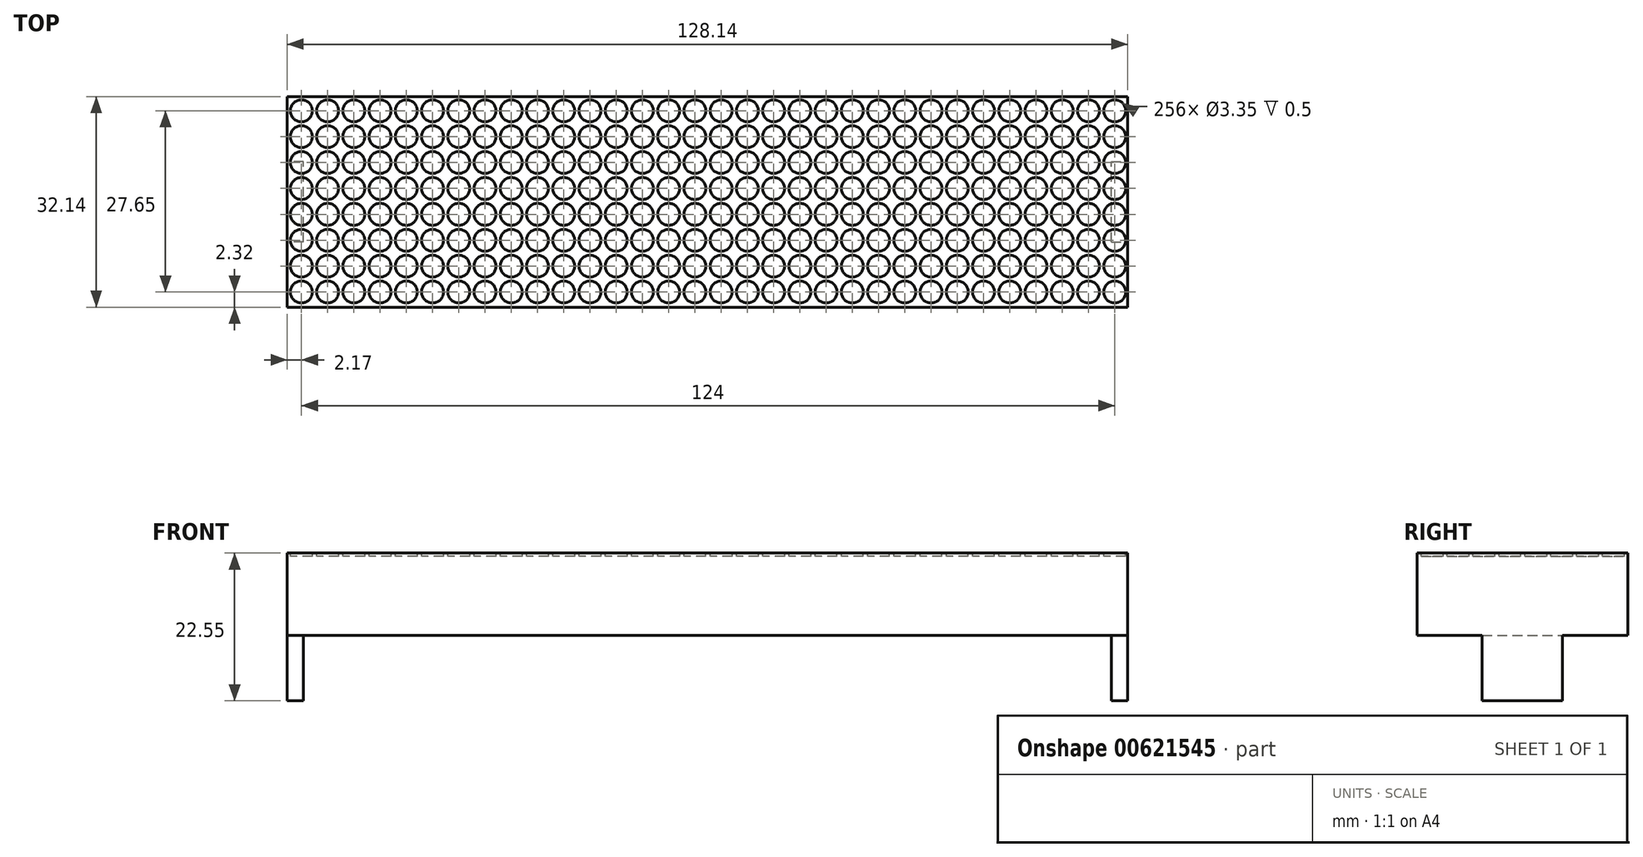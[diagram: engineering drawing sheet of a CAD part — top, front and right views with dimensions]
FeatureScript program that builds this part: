
annotation { "Feature Type Name" : "Feature", "Feature Type Description" : "" }
export const myFeature = defineFeature(function(context is Context, id is Id, definition is map)
    precondition{}
    {
        {
            var Q0;
            Q0=qCreatedBy(makeId("Top.planeOp"),FACE);
            var sketch = newSketch(context, id + "F0", { "sketchPlane" : qUnion([Q0])});
            skLineSegment(sketch, "E0.bottom", {"start": v(64.08, -16.07) * mm, "end": v(-64.08, -16.08) * mm});
            skLineSegment(sketch, "E0.top", {"start": v(64.08, 16.08) * mm, "end": v(-64.08, 16.07) * mm});
            skLineSegment(sketch, "E0.left", {"start": v(64.08, -16.07) * mm, "end": v(64.08, 16.08) * mm});
            skLineSegment(sketch, "E0.right", {"start": v(-64.08, -16.08) * mm, "end": v(-64.08, 16.07) * mm});
            skPoint(sketch, "E0.middle", {"position": v(0, 0) * mm});
            skSolve(sketch);
        }
        {
            var Q0;
            Q0=makeQuery(id+"F0.imprint","IMPRINT",FACE,{"disambiguationData":[TD([[makeQuery(id+"F0.imprint","IMPRINT",EDGE,{"derivedFrom":sQuery(id+"F0.wireOp",EDGE,"E0.bottom")}),-1.0]])]});
            extrude(context, id + "F1", {"entities" : qUnion([Q0]), "depth" : 12.55 * mm, "offsetDistance" : 25 * mm});
        }
        {
            var Q0;
            Q0=makeQuery(id+"F1.opExtrude","CAP_FACE",FACE,{"disambiguationData":[OSD([sQuery(id+"F0.wireOp",EDGE,"E0.bottom"),sQuery(id+"F0.wireOp",EDGE,"E0.top"),sQuery(id+"F0.wireOp",EDGE,"E0.left"),sQuery(id+"F0.wireOp",EDGE,"E0.right")])],"isStart":true});
            var sketch = newSketch(context, id + "F2", { "sketchPlane" : qUnion([Q0])});
            skLineSegment(sketch, "E1.bottom", {"start": v(-61.58, 6.12) * mm, "end": v(-64.08, 6.12) * mm});
            skLineSegment(sketch, "E1.top", {"start": v(-61.58, -6.13) * mm, "end": v(-64.08, -6.13) * mm});
            skLineSegment(sketch, "E1.left", {"start": v(-61.58, 6.12) * mm, "end": v(-61.58, -6.13) * mm});
            skLineSegment(sketch, "E1.right", {"start": v(-64.08, 6.12) * mm, "end": v(-64.08, -6.13) * mm});
            skPoint(sketch, "E1.middle", {"position": v(-62.83, 0) * mm});
            skPoint(sketch, "E2.MirrorP", {"position": v(62.83, 0) * mm});
            skLineSegment(sketch, "E3.MirrorCS", {"start": v(61.58, 6.12) * mm, "end": v(64.08, 6.12) * mm});
            skLineSegment(sketch, "E4.MirrorCS", {"start": v(61.58, -6.13) * mm, "end": v(64.08, -6.13) * mm});
            skLineSegment(sketch, "E5.MirrorCS", {"start": v(61.58, 6.12) * mm, "end": v(61.58, -6.13) * mm});
            skLineSegment(sketch, "E6.MirrorCS", {"start": v(64.08, 6.12) * mm, "end": v(64.08, -6.13) * mm});
            skSolve(sketch);
        }
        {
            var Q0;
            Q0 = qSketchRegion(id + "F2", true);
            extrude(context, id + "F3", {"entities" : qUnion([Q0]), "operationType" : NewBodyOperationType.ADD, "depth" : 10 * mm, "offsetDistance" : 25 * mm});
        }
        {
            var Q0;
            Q0=makeQuery(id+"F1.opExtrude","CAP_FACE",FACE,{"disambiguationData":[OSD([sQuery(id+"F0.wireOp",EDGE,"E0.bottom"),sQuery(id+"F0.wireOp",EDGE,"E0.top"),sQuery(id+"F0.wireOp",EDGE,"E0.left"),sQuery(id+"F0.wireOp",EDGE,"E0.right")])],"isStart":false});
            var sketch = newSketch(context, id + "F4", { "sketchPlane" : qUnion([Q0])});
            skCircle(sketch, "E7", {"center": v(-61.9, 13.9) * mm, "radius": 1.68 * mm});
            skCircle(sketch, "E8.0.1.0", {"center": v(-61.9, 9.95) * mm, "radius": 1.68 * mm});
            skCircle(sketch, "E8.0.2.0", {"center": v(-61.9, 6) * mm, "radius": 1.68 * mm});
            skCircle(sketch, "E8.0.3.0", {"center": v(-61.9, 2.05) * mm, "radius": 1.68 * mm});
            skCircle(sketch, "E8.0.4.0", {"center": v(-61.9, -1.9) * mm, "radius": 1.68 * mm});
            skCircle(sketch, "E8.0.5.0", {"center": v(-61.9, -5.85) * mm, "radius": 1.68 * mm});
            skCircle(sketch, "E8.0.6.0", {"center": v(-61.9, -9.8) * mm, "radius": 1.68 * mm});
            skCircle(sketch, "E8.0.7.0", {"center": v(-61.9, -13.75) * mm, "radius": 1.68 * mm});
            skCircle(sketch, "E8.1.0.0", {"center": v(-57.9, 13.9) * mm, "radius": 1.68 * mm});
            skCircle(sketch, "E8.1.1.0", {"center": v(-57.9, 9.95) * mm, "radius": 1.68 * mm});
            skCircle(sketch, "E8.1.2.0", {"center": v(-57.9, 6) * mm, "radius": 1.68 * mm});
            skCircle(sketch, "E8.1.3.0", {"center": v(-57.9, 2.05) * mm, "radius": 1.68 * mm});
            skCircle(sketch, "E8.1.4.0", {"center": v(-57.9, -1.9) * mm, "radius": 1.68 * mm});
            skCircle(sketch, "E8.1.5.0", {"center": v(-57.9, -5.85) * mm, "radius": 1.68 * mm});
            skCircle(sketch, "E8.1.6.0", {"center": v(-57.9, -9.8) * mm, "radius": 1.68 * mm});
            skCircle(sketch, "E8.1.7.0", {"center": v(-57.9, -13.75) * mm, "radius": 1.68 * mm});
            skCircle(sketch, "E8.2.0.0", {"center": v(-53.9, 13.9) * mm, "radius": 1.68 * mm});
            skCircle(sketch, "E8.2.1.0", {"center": v(-53.9, 9.95) * mm, "radius": 1.68 * mm});
            skCircle(sketch, "E8.2.2.0", {"center": v(-53.9, 6) * mm, "radius": 1.68 * mm});
            skCircle(sketch, "E8.2.3.0", {"center": v(-53.9, 2.05) * mm, "radius": 1.68 * mm});
            skCircle(sketch, "E8.2.4.0", {"center": v(-53.9, -1.9) * mm, "radius": 1.68 * mm});
            skCircle(sketch, "E8.2.5.0", {"center": v(-53.9, -5.85) * mm, "radius": 1.68 * mm});
            skCircle(sketch, "E8.2.6.0", {"center": v(-53.9, -9.8) * mm, "radius": 1.68 * mm});
            skCircle(sketch, "E8.2.7.0", {"center": v(-53.9, -13.75) * mm, "radius": 1.68 * mm});
            skLineSegment(sketch, "E8.direction1", {"start": v(-61.9, 13.9) * mm, "end": v(-57.9, 13.9) * mm, "construction": true});
            skLineSegment(sketch, "E8.direction2", {"start": v(-61.9, 13.9) * mm, "end": v(-61.9, 9.95) * mm, "construction": true});
            skCircle(sketch, "E9.0.3.0", {"center": v(-49.9, 13.9) * mm, "radius": 1.68 * mm});
            skCircle(sketch, "E9.0.3.1", {"center": v(-49.9, 9.95) * mm, "radius": 1.68 * mm});
            skCircle(sketch, "E9.0.3.2", {"center": v(-49.9, 6) * mm, "radius": 1.68 * mm});
            skCircle(sketch, "E9.0.3.3", {"center": v(-49.9, 2.05) * mm, "radius": 1.68 * mm});
            skCircle(sketch, "E9.0.3.4", {"center": v(-49.9, -1.9) * mm, "radius": 1.68 * mm});
            skCircle(sketch, "E9.0.3.5", {"center": v(-49.9, -5.85) * mm, "radius": 1.68 * mm});
            skCircle(sketch, "E9.0.3.6", {"center": v(-49.9, -9.8) * mm, "radius": 1.68 * mm});
            skCircle(sketch, "E9.0.3.7", {"center": v(-49.9, -13.75) * mm, "radius": 1.68 * mm});
            skCircle(sketch, "E9.0.4.0", {"center": v(-45.9, 13.9) * mm, "radius": 1.68 * mm});
            skCircle(sketch, "E9.0.4.1", {"center": v(-45.9, 9.95) * mm, "radius": 1.68 * mm});
            skCircle(sketch, "E9.0.4.2", {"center": v(-45.9, 6) * mm, "radius": 1.68 * mm});
            skCircle(sketch, "E9.0.4.3", {"center": v(-45.9, 2.05) * mm, "radius": 1.68 * mm});
            skCircle(sketch, "E9.0.4.4", {"center": v(-45.9, -1.9) * mm, "radius": 1.68 * mm});
            skCircle(sketch, "E9.0.4.5", {"center": v(-45.9, -5.85) * mm, "radius": 1.68 * mm});
            skCircle(sketch, "E9.0.4.6", {"center": v(-45.9, -9.8) * mm, "radius": 1.68 * mm});
            skCircle(sketch, "E9.0.4.7", {"center": v(-45.9, -13.75) * mm, "radius": 1.68 * mm});
            skCircle(sketch, "E9.0.5.0", {"center": v(-41.9, 13.9) * mm, "radius": 1.68 * mm});
            skCircle(sketch, "E9.0.5.1", {"center": v(-41.9, 9.95) * mm, "radius": 1.68 * mm});
            skCircle(sketch, "E9.0.5.2", {"center": v(-41.9, 6) * mm, "radius": 1.68 * mm});
            skCircle(sketch, "E9.0.5.3", {"center": v(-41.9, 2.05) * mm, "radius": 1.68 * mm});
            skCircle(sketch, "E9.0.5.4", {"center": v(-41.9, -1.9) * mm, "radius": 1.68 * mm});
            skCircle(sketch, "E9.0.5.5", {"center": v(-41.9, -5.85) * mm, "radius": 1.68 * mm});
            skCircle(sketch, "E9.0.5.6", {"center": v(-41.9, -9.8) * mm, "radius": 1.68 * mm});
            skCircle(sketch, "E9.0.5.7", {"center": v(-41.9, -13.75) * mm, "radius": 1.68 * mm});
            skCircle(sketch, "E9.0.6.0", {"center": v(-37.9, 13.9) * mm, "radius": 1.68 * mm});
            skCircle(sketch, "E9.0.6.1", {"center": v(-37.9, 9.95) * mm, "radius": 1.68 * mm});
            skCircle(sketch, "E9.0.6.2", {"center": v(-37.9, 6) * mm, "radius": 1.68 * mm});
            skCircle(sketch, "E9.0.6.3", {"center": v(-37.9, 2.05) * mm, "radius": 1.68 * mm});
            skCircle(sketch, "E9.0.6.4", {"center": v(-37.9, -1.9) * mm, "radius": 1.68 * mm});
            skCircle(sketch, "E9.0.6.5", {"center": v(-37.9, -5.85) * mm, "radius": 1.68 * mm});
            skCircle(sketch, "E9.0.6.6", {"center": v(-37.9, -9.8) * mm, "radius": 1.68 * mm});
            skCircle(sketch, "E9.0.6.7", {"center": v(-37.9, -13.75) * mm, "radius": 1.68 * mm});
            skCircle(sketch, "E9.0.7.0", {"center": v(-33.9, 13.9) * mm, "radius": 1.68 * mm});
            skCircle(sketch, "E9.0.7.1", {"center": v(-33.9, 9.95) * mm, "radius": 1.68 * mm});
            skCircle(sketch, "E9.0.7.2", {"center": v(-33.9, 6) * mm, "radius": 1.68 * mm});
            skCircle(sketch, "E9.0.7.3", {"center": v(-33.9, 2.05) * mm, "radius": 1.68 * mm});
            skCircle(sketch, "E9.0.7.4", {"center": v(-33.9, -1.9) * mm, "radius": 1.68 * mm});
            skCircle(sketch, "E9.0.7.5", {"center": v(-33.9, -5.85) * mm, "radius": 1.68 * mm});
            skCircle(sketch, "E9.0.7.6", {"center": v(-33.9, -9.8) * mm, "radius": 1.68 * mm});
            skCircle(sketch, "E9.0.7.7", {"center": v(-33.9, -13.75) * mm, "radius": 1.68 * mm});
            skCircle(sketch, "E9.0.8.0", {"center": v(-29.9, 13.9) * mm, "radius": 1.68 * mm});
            skCircle(sketch, "E9.0.8.1", {"center": v(-29.9, 9.95) * mm, "radius": 1.68 * mm});
            skCircle(sketch, "E9.0.8.2", {"center": v(-29.9, 6) * mm, "radius": 1.68 * mm});
            skCircle(sketch, "E9.0.8.3", {"center": v(-29.9, 2.05) * mm, "radius": 1.68 * mm});
            skCircle(sketch, "E9.0.8.4", {"center": v(-29.9, -1.9) * mm, "radius": 1.68 * mm});
            skCircle(sketch, "E9.0.8.5", {"center": v(-29.9, -5.85) * mm, "radius": 1.68 * mm});
            skCircle(sketch, "E9.0.8.6", {"center": v(-29.9, -9.8) * mm, "radius": 1.68 * mm});
            skCircle(sketch, "E9.0.8.7", {"center": v(-29.9, -13.75) * mm, "radius": 1.68 * mm});
            skCircle(sketch, "E9.0.9.0", {"center": v(-25.9, 13.9) * mm, "radius": 1.68 * mm});
            skCircle(sketch, "E9.0.9.1", {"center": v(-25.9, 9.95) * mm, "radius": 1.68 * mm});
            skCircle(sketch, "E9.0.9.2", {"center": v(-25.9, 6) * mm, "radius": 1.68 * mm});
            skCircle(sketch, "E9.0.9.3", {"center": v(-25.9, 2.05) * mm, "radius": 1.68 * mm});
            skCircle(sketch, "E9.0.9.4", {"center": v(-25.9, -1.9) * mm, "radius": 1.68 * mm});
            skCircle(sketch, "E9.0.9.5", {"center": v(-25.9, -5.85) * mm, "radius": 1.68 * mm});
            skCircle(sketch, "E9.0.9.6", {"center": v(-25.9, -9.8) * mm, "radius": 1.68 * mm});
            skCircle(sketch, "E9.0.9.7", {"center": v(-25.9, -13.75) * mm, "radius": 1.68 * mm});
            skCircle(sketch, "E9.0.10.0", {"center": v(-21.9, 13.9) * mm, "radius": 1.68 * mm});
            skCircle(sketch, "E9.0.10.1", {"center": v(-21.9, 9.95) * mm, "radius": 1.68 * mm});
            skCircle(sketch, "E9.0.10.2", {"center": v(-21.9, 6) * mm, "radius": 1.68 * mm});
            skCircle(sketch, "E9.0.10.3", {"center": v(-21.9, 2.05) * mm, "radius": 1.68 * mm});
            skCircle(sketch, "E9.0.10.4", {"center": v(-21.9, -1.9) * mm, "radius": 1.68 * mm});
            skCircle(sketch, "E9.0.10.5", {"center": v(-21.9, -5.85) * mm, "radius": 1.68 * mm});
            skCircle(sketch, "E9.0.10.6", {"center": v(-21.9, -9.8) * mm, "radius": 1.68 * mm});
            skCircle(sketch, "E9.0.10.7", {"center": v(-21.9, -13.75) * mm, "radius": 1.68 * mm});
            skCircle(sketch, "E9.0.11.0", {"center": v(-17.9, 13.9) * mm, "radius": 1.68 * mm});
            skCircle(sketch, "E9.0.11.1", {"center": v(-17.9, 9.95) * mm, "radius": 1.68 * mm});
            skCircle(sketch, "E9.0.11.2", {"center": v(-17.9, 6) * mm, "radius": 1.68 * mm});
            skCircle(sketch, "E9.0.11.3", {"center": v(-17.9, 2.05) * mm, "radius": 1.68 * mm});
            skCircle(sketch, "E9.0.11.4", {"center": v(-17.9, -1.9) * mm, "radius": 1.68 * mm});
            skCircle(sketch, "E9.0.11.5", {"center": v(-17.9, -5.85) * mm, "radius": 1.68 * mm});
            skCircle(sketch, "E9.0.11.6", {"center": v(-17.9, -9.8) * mm, "radius": 1.68 * mm});
            skCircle(sketch, "E9.0.11.7", {"center": v(-17.9, -13.75) * mm, "radius": 1.68 * mm});
            skCircle(sketch, "E9.0.12.0", {"center": v(-13.9, 13.9) * mm, "radius": 1.68 * mm});
            skCircle(sketch, "E9.0.12.1", {"center": v(-13.9, 9.95) * mm, "radius": 1.68 * mm});
            skCircle(sketch, "E9.0.12.2", {"center": v(-13.9, 6) * mm, "radius": 1.68 * mm});
            skCircle(sketch, "E9.0.12.3", {"center": v(-13.9, 2.05) * mm, "radius": 1.68 * mm});
            skCircle(sketch, "E9.0.12.4", {"center": v(-13.9, -1.9) * mm, "radius": 1.68 * mm});
            skCircle(sketch, "E9.0.12.5", {"center": v(-13.9, -5.85) * mm, "radius": 1.68 * mm});
            skCircle(sketch, "E9.0.12.6", {"center": v(-13.9, -9.8) * mm, "radius": 1.68 * mm});
            skCircle(sketch, "E9.0.12.7", {"center": v(-13.9, -13.75) * mm, "radius": 1.68 * mm});
            skCircle(sketch, "E9.0.13.0", {"center": v(-9.9, 13.9) * mm, "radius": 1.68 * mm});
            skCircle(sketch, "E9.0.13.1", {"center": v(-9.9, 9.95) * mm, "radius": 1.68 * mm});
            skCircle(sketch, "E9.0.13.2", {"center": v(-9.9, 6) * mm, "radius": 1.68 * mm});
            skCircle(sketch, "E9.0.13.3", {"center": v(-9.9, 2.05) * mm, "radius": 1.68 * mm});
            skCircle(sketch, "E9.0.13.4", {"center": v(-9.9, -1.9) * mm, "radius": 1.68 * mm});
            skCircle(sketch, "E9.0.13.5", {"center": v(-9.9, -5.85) * mm, "radius": 1.68 * mm});
            skCircle(sketch, "E9.0.13.6", {"center": v(-9.9, -9.8) * mm, "radius": 1.68 * mm});
            skCircle(sketch, "E9.0.13.7", {"center": v(-9.9, -13.75) * mm, "radius": 1.68 * mm});
            skCircle(sketch, "E9.0.14.0", {"center": v(-5.9, 13.9) * mm, "radius": 1.68 * mm});
            skCircle(sketch, "E9.0.14.1", {"center": v(-5.9, 9.95) * mm, "radius": 1.68 * mm});
            skCircle(sketch, "E9.0.14.2", {"center": v(-5.9, 6) * mm, "radius": 1.68 * mm});
            skCircle(sketch, "E9.0.14.3", {"center": v(-5.9, 2.05) * mm, "radius": 1.68 * mm});
            skCircle(sketch, "E9.0.14.4", {"center": v(-5.9, -1.9) * mm, "radius": 1.68 * mm});
            skCircle(sketch, "E9.0.14.5", {"center": v(-5.9, -5.85) * mm, "radius": 1.68 * mm});
            skCircle(sketch, "E9.0.14.6", {"center": v(-5.9, -9.8) * mm, "radius": 1.68 * mm});
            skCircle(sketch, "E9.0.14.7", {"center": v(-5.9, -13.75) * mm, "radius": 1.68 * mm});
            skCircle(sketch, "E9.0.15.0", {"center": v(-1.9, 13.9) * mm, "radius": 1.68 * mm});
            skCircle(sketch, "E9.0.15.1", {"center": v(-1.9, 9.95) * mm, "radius": 1.68 * mm});
            skCircle(sketch, "E9.0.15.2", {"center": v(-1.9, 6) * mm, "radius": 1.68 * mm});
            skCircle(sketch, "E9.0.15.3", {"center": v(-1.9, 2.05) * mm, "radius": 1.68 * mm});
            skCircle(sketch, "E9.0.15.4", {"center": v(-1.9, -1.9) * mm, "radius": 1.68 * mm});
            skCircle(sketch, "E9.0.15.5", {"center": v(-1.9, -5.85) * mm, "radius": 1.68 * mm});
            skCircle(sketch, "E9.0.15.6", {"center": v(-1.9, -9.8) * mm, "radius": 1.68 * mm});
            skCircle(sketch, "E9.0.15.7", {"center": v(-1.9, -13.75) * mm, "radius": 1.68 * mm});
            skCircle(sketch, "E9.0.16.0", {"center": v(2.1, 13.9) * mm, "radius": 1.68 * mm});
            skCircle(sketch, "E9.0.16.1", {"center": v(2.1, 9.95) * mm, "radius": 1.68 * mm});
            skCircle(sketch, "E9.0.16.2", {"center": v(2.1, 6) * mm, "radius": 1.68 * mm});
            skCircle(sketch, "E9.0.16.3", {"center": v(2.1, 2.05) * mm, "radius": 1.68 * mm});
            skCircle(sketch, "E9.0.16.4", {"center": v(2.1, -1.9) * mm, "radius": 1.68 * mm});
            skCircle(sketch, "E9.0.16.5", {"center": v(2.1, -5.85) * mm, "radius": 1.68 * mm});
            skCircle(sketch, "E9.0.16.6", {"center": v(2.1, -9.8) * mm, "radius": 1.68 * mm});
            skCircle(sketch, "E9.0.16.7", {"center": v(2.1, -13.75) * mm, "radius": 1.68 * mm});
            skCircle(sketch, "E9.0.17.0", {"center": v(6.1, 13.9) * mm, "radius": 1.68 * mm});
            skCircle(sketch, "E9.0.17.1", {"center": v(6.1, 9.95) * mm, "radius": 1.68 * mm});
            skCircle(sketch, "E9.0.17.2", {"center": v(6.1, 6) * mm, "radius": 1.68 * mm});
            skCircle(sketch, "E9.0.17.3", {"center": v(6.1, 2.05) * mm, "radius": 1.68 * mm});
            skCircle(sketch, "E9.0.17.4", {"center": v(6.1, -1.9) * mm, "radius": 1.68 * mm});
            skCircle(sketch, "E9.0.17.5", {"center": v(6.1, -5.85) * mm, "radius": 1.68 * mm});
            skCircle(sketch, "E9.0.17.6", {"center": v(6.1, -9.8) * mm, "radius": 1.68 * mm});
            skCircle(sketch, "E9.0.17.7", {"center": v(6.1, -13.75) * mm, "radius": 1.68 * mm});
            skCircle(sketch, "E9.0.18.0", {"center": v(10.1, 13.9) * mm, "radius": 1.68 * mm});
            skCircle(sketch, "E9.0.18.1", {"center": v(10.1, 9.95) * mm, "radius": 1.68 * mm});
            skCircle(sketch, "E9.0.18.2", {"center": v(10.1, 6) * mm, "radius": 1.68 * mm});
            skCircle(sketch, "E9.0.18.3", {"center": v(10.1, 2.05) * mm, "radius": 1.68 * mm});
            skCircle(sketch, "E9.0.18.4", {"center": v(10.1, -1.9) * mm, "radius": 1.68 * mm});
            skCircle(sketch, "E9.0.18.5", {"center": v(10.1, -5.85) * mm, "radius": 1.68 * mm});
            skCircle(sketch, "E9.0.18.6", {"center": v(10.1, -9.8) * mm, "radius": 1.68 * mm});
            skCircle(sketch, "E9.0.18.7", {"center": v(10.1, -13.75) * mm, "radius": 1.68 * mm});
            skCircle(sketch, "E9.0.19.0", {"center": v(14.1, 13.9) * mm, "radius": 1.68 * mm});
            skCircle(sketch, "E9.0.19.1", {"center": v(14.1, 9.95) * mm, "radius": 1.68 * mm});
            skCircle(sketch, "E9.0.19.2", {"center": v(14.1, 6) * mm, "radius": 1.68 * mm});
            skCircle(sketch, "E9.0.19.3", {"center": v(14.1, 2.05) * mm, "radius": 1.68 * mm});
            skCircle(sketch, "E9.0.19.4", {"center": v(14.1, -1.9) * mm, "radius": 1.68 * mm});
            skCircle(sketch, "E9.0.19.5", {"center": v(14.1, -5.85) * mm, "radius": 1.68 * mm});
            skCircle(sketch, "E9.0.19.6", {"center": v(14.1, -9.8) * mm, "radius": 1.68 * mm});
            skCircle(sketch, "E9.0.19.7", {"center": v(14.1, -13.75) * mm, "radius": 1.68 * mm});
            skCircle(sketch, "E9.0.20.0", {"center": v(18.1, 13.9) * mm, "radius": 1.68 * mm});
            skCircle(sketch, "E9.0.20.1", {"center": v(18.1, 9.95) * mm, "radius": 1.68 * mm});
            skCircle(sketch, "E9.0.20.2", {"center": v(18.1, 6) * mm, "radius": 1.68 * mm});
            skCircle(sketch, "E9.0.20.3", {"center": v(18.1, 2.05) * mm, "radius": 1.68 * mm});
            skCircle(sketch, "E9.0.20.4", {"center": v(18.1, -1.9) * mm, "radius": 1.68 * mm});
            skCircle(sketch, "E9.0.20.5", {"center": v(18.1, -5.85) * mm, "radius": 1.68 * mm});
            skCircle(sketch, "E9.0.20.6", {"center": v(18.1, -9.8) * mm, "radius": 1.68 * mm});
            skCircle(sketch, "E9.0.20.7", {"center": v(18.1, -13.75) * mm, "radius": 1.68 * mm});
            skCircle(sketch, "E9.0.21.0", {"center": v(22.1, 13.9) * mm, "radius": 1.68 * mm});
            skCircle(sketch, "E9.0.21.1", {"center": v(22.1, 9.95) * mm, "radius": 1.68 * mm});
            skCircle(sketch, "E9.0.21.2", {"center": v(22.1, 6) * mm, "radius": 1.68 * mm});
            skCircle(sketch, "E9.0.21.3", {"center": v(22.1, 2.05) * mm, "radius": 1.68 * mm});
            skCircle(sketch, "E9.0.21.4", {"center": v(22.1, -1.9) * mm, "radius": 1.68 * mm});
            skCircle(sketch, "E9.0.21.5", {"center": v(22.1, -5.85) * mm, "radius": 1.68 * mm});
            skCircle(sketch, "E9.0.21.6", {"center": v(22.1, -9.8) * mm, "radius": 1.68 * mm});
            skCircle(sketch, "E9.0.21.7", {"center": v(22.1, -13.75) * mm, "radius": 1.68 * mm});
            skCircle(sketch, "E9.0.22.0", {"center": v(26.1, 13.9) * mm, "radius": 1.68 * mm});
            skCircle(sketch, "E9.0.22.1", {"center": v(26.1, 9.95) * mm, "radius": 1.68 * mm});
            skCircle(sketch, "E9.0.22.2", {"center": v(26.1, 6) * mm, "radius": 1.68 * mm});
            skCircle(sketch, "E9.0.22.3", {"center": v(26.1, 2.05) * mm, "radius": 1.68 * mm});
            skCircle(sketch, "E9.0.22.4", {"center": v(26.1, -1.9) * mm, "radius": 1.68 * mm});
            skCircle(sketch, "E9.0.22.5", {"center": v(26.1, -5.85) * mm, "radius": 1.68 * mm});
            skCircle(sketch, "E9.0.22.6", {"center": v(26.1, -9.8) * mm, "radius": 1.68 * mm});
            skCircle(sketch, "E9.0.22.7", {"center": v(26.1, -13.75) * mm, "radius": 1.68 * mm});
            skCircle(sketch, "E9.0.23.0", {"center": v(30.1, 13.9) * mm, "radius": 1.68 * mm});
            skCircle(sketch, "E9.0.23.1", {"center": v(30.1, 9.95) * mm, "radius": 1.68 * mm});
            skCircle(sketch, "E9.0.23.2", {"center": v(30.1, 6) * mm, "radius": 1.68 * mm});
            skCircle(sketch, "E9.0.23.3", {"center": v(30.1, 2.05) * mm, "radius": 1.68 * mm});
            skCircle(sketch, "E9.0.23.4", {"center": v(30.1, -1.9) * mm, "radius": 1.68 * mm});
            skCircle(sketch, "E9.0.23.5", {"center": v(30.1, -5.85) * mm, "radius": 1.68 * mm});
            skCircle(sketch, "E9.0.23.6", {"center": v(30.1, -9.8) * mm, "radius": 1.68 * mm});
            skCircle(sketch, "E9.0.23.7", {"center": v(30.1, -13.75) * mm, "radius": 1.68 * mm});
            skCircle(sketch, "E9.0.24.0", {"center": v(34.1, 13.9) * mm, "radius": 1.68 * mm});
            skCircle(sketch, "E9.0.24.1", {"center": v(34.1, 9.95) * mm, "radius": 1.68 * mm});
            skCircle(sketch, "E9.0.24.2", {"center": v(34.1, 6) * mm, "radius": 1.68 * mm});
            skCircle(sketch, "E9.0.24.3", {"center": v(34.1, 2.05) * mm, "radius": 1.68 * mm});
            skCircle(sketch, "E9.0.24.4", {"center": v(34.1, -1.9) * mm, "radius": 1.68 * mm});
            skCircle(sketch, "E9.0.24.5", {"center": v(34.1, -5.85) * mm, "radius": 1.68 * mm});
            skCircle(sketch, "E9.0.24.6", {"center": v(34.1, -9.8) * mm, "radius": 1.68 * mm});
            skCircle(sketch, "E9.0.24.7", {"center": v(34.1, -13.75) * mm, "radius": 1.68 * mm});
            skCircle(sketch, "E9.0.25.0", {"center": v(38.1, 13.9) * mm, "radius": 1.68 * mm});
            skCircle(sketch, "E9.0.25.1", {"center": v(38.1, 9.95) * mm, "radius": 1.68 * mm});
            skCircle(sketch, "E9.0.25.2", {"center": v(38.1, 6) * mm, "radius": 1.68 * mm});
            skCircle(sketch, "E9.0.25.3", {"center": v(38.1, 2.05) * mm, "radius": 1.68 * mm});
            skCircle(sketch, "E9.0.25.4", {"center": v(38.1, -1.9) * mm, "radius": 1.68 * mm});
            skCircle(sketch, "E9.0.25.5", {"center": v(38.1, -5.85) * mm, "radius": 1.68 * mm});
            skCircle(sketch, "E9.0.25.6", {"center": v(38.1, -9.8) * mm, "radius": 1.68 * mm});
            skCircle(sketch, "E9.0.25.7", {"center": v(38.1, -13.75) * mm, "radius": 1.68 * mm});
            skCircle(sketch, "E9.0.26.0", {"center": v(42.1, 13.9) * mm, "radius": 1.68 * mm});
            skCircle(sketch, "E9.0.26.1", {"center": v(42.1, 9.95) * mm, "radius": 1.68 * mm});
            skCircle(sketch, "E9.0.26.2", {"center": v(42.1, 6) * mm, "radius": 1.68 * mm});
            skCircle(sketch, "E9.0.26.3", {"center": v(42.1, 2.05) * mm, "radius": 1.68 * mm});
            skCircle(sketch, "E9.0.26.4", {"center": v(42.1, -1.9) * mm, "radius": 1.68 * mm});
            skCircle(sketch, "E9.0.26.5", {"center": v(42.1, -5.85) * mm, "radius": 1.68 * mm});
            skCircle(sketch, "E9.0.26.6", {"center": v(42.1, -9.8) * mm, "radius": 1.68 * mm});
            skCircle(sketch, "E9.0.26.7", {"center": v(42.1, -13.75) * mm, "radius": 1.68 * mm});
            skCircle(sketch, "E9.0.27.0", {"center": v(46.1, 13.9) * mm, "radius": 1.68 * mm});
            skCircle(sketch, "E9.0.27.1", {"center": v(46.1, 9.95) * mm, "radius": 1.68 * mm});
            skCircle(sketch, "E9.0.27.2", {"center": v(46.1, 6) * mm, "radius": 1.68 * mm});
            skCircle(sketch, "E9.0.27.3", {"center": v(46.1, 2.05) * mm, "radius": 1.68 * mm});
            skCircle(sketch, "E9.0.27.4", {"center": v(46.1, -1.9) * mm, "radius": 1.68 * mm});
            skCircle(sketch, "E9.0.27.5", {"center": v(46.1, -5.85) * mm, "radius": 1.68 * mm});
            skCircle(sketch, "E9.0.27.6", {"center": v(46.1, -9.8) * mm, "radius": 1.68 * mm});
            skCircle(sketch, "E9.0.27.7", {"center": v(46.1, -13.75) * mm, "radius": 1.68 * mm});
            skCircle(sketch, "E9.0.28.0", {"center": v(50.1, 13.9) * mm, "radius": 1.68 * mm});
            skCircle(sketch, "E9.0.28.1", {"center": v(50.1, 9.95) * mm, "radius": 1.68 * mm});
            skCircle(sketch, "E9.0.28.2", {"center": v(50.1, 6) * mm, "radius": 1.68 * mm});
            skCircle(sketch, "E9.0.28.3", {"center": v(50.1, 2.05) * mm, "radius": 1.68 * mm});
            skCircle(sketch, "E9.0.28.4", {"center": v(50.1, -1.9) * mm, "radius": 1.68 * mm});
            skCircle(sketch, "E9.0.28.5", {"center": v(50.1, -5.85) * mm, "radius": 1.68 * mm});
            skCircle(sketch, "E9.0.28.6", {"center": v(50.1, -9.8) * mm, "radius": 1.68 * mm});
            skCircle(sketch, "E9.0.28.7", {"center": v(50.1, -13.75) * mm, "radius": 1.68 * mm});
            skCircle(sketch, "E9.0.29.0", {"center": v(54.1, 13.9) * mm, "radius": 1.68 * mm});
            skCircle(sketch, "E9.0.29.1", {"center": v(54.1, 9.95) * mm, "radius": 1.68 * mm});
            skCircle(sketch, "E9.0.29.2", {"center": v(54.1, 6) * mm, "radius": 1.68 * mm});
            skCircle(sketch, "E9.0.29.3", {"center": v(54.1, 2.05) * mm, "radius": 1.68 * mm});
            skCircle(sketch, "E9.0.29.4", {"center": v(54.1, -1.9) * mm, "radius": 1.68 * mm});
            skCircle(sketch, "E9.0.29.5", {"center": v(54.1, -5.85) * mm, "radius": 1.68 * mm});
            skCircle(sketch, "E9.0.29.6", {"center": v(54.1, -9.8) * mm, "radius": 1.68 * mm});
            skCircle(sketch, "E9.0.29.7", {"center": v(54.1, -13.75) * mm, "radius": 1.68 * mm});
            skCircle(sketch, "E9.0.30.0", {"center": v(58.1, 13.9) * mm, "radius": 1.68 * mm});
            skCircle(sketch, "E9.0.30.1", {"center": v(58.1, 9.95) * mm, "radius": 1.68 * mm});
            skCircle(sketch, "E9.0.30.2", {"center": v(58.1, 6) * mm, "radius": 1.68 * mm});
            skCircle(sketch, "E9.0.30.3", {"center": v(58.1, 2.05) * mm, "radius": 1.68 * mm});
            skCircle(sketch, "E9.0.30.4", {"center": v(58.1, -1.9) * mm, "radius": 1.68 * mm});
            skCircle(sketch, "E9.0.30.5", {"center": v(58.1, -5.85) * mm, "radius": 1.68 * mm});
            skCircle(sketch, "E9.0.30.6", {"center": v(58.1, -9.8) * mm, "radius": 1.68 * mm});
            skCircle(sketch, "E9.0.30.7", {"center": v(58.1, -13.75) * mm, "radius": 1.68 * mm});
            skCircle(sketch, "E9.0.31.0", {"center": v(62.1, 13.9) * mm, "radius": 1.68 * mm});
            skCircle(sketch, "E9.0.31.1", {"center": v(62.1, 9.95) * mm, "radius": 1.68 * mm});
            skCircle(sketch, "E9.0.31.2", {"center": v(62.1, 6) * mm, "radius": 1.68 * mm});
            skCircle(sketch, "E9.0.31.3", {"center": v(62.1, 2.05) * mm, "radius": 1.68 * mm});
            skCircle(sketch, "E9.0.31.4", {"center": v(62.1, -1.9) * mm, "radius": 1.68 * mm});
            skCircle(sketch, "E9.0.31.5", {"center": v(62.1, -5.85) * mm, "radius": 1.68 * mm});
            skCircle(sketch, "E9.0.31.6", {"center": v(62.1, -9.8) * mm, "radius": 1.68 * mm});
            skCircle(sketch, "E9.0.31.7", {"center": v(62.1, -13.75) * mm, "radius": 1.68 * mm});
            skSolve(sketch);
        }
        {
            var Q0;
            Q0 = qSketchRegion(id + "F4", true);
            extrude(context, id + "F5", {"entities" : qUnion([Q0]), "operationType" : NewBodyOperationType.REMOVE, "oppositeDirection" : true, "depth" : 0.5 * mm, "offsetDistance" : 25 * mm});
        }
    });
